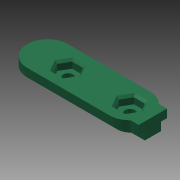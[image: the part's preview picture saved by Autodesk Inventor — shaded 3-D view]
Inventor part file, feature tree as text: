
AUTODESK INVENTOR PART (.ipt)
format: ipt  version: 2014 (Build 180170000, 170)  size: 260,096 bytes
history: native  units: in
note: dims shown in document units (in); Inventor stores cm internally (conversion verified against a paired STEP export)
features: extrude x7, sketch x7, plane x2, chamfer x2, mirror x1, projected_geometry x1
ambient origin geometry x8: Origin, YZ Plane, XZ Plane, XY Plane, X Axis, Y Axis, Z Axis, Center Point
bodies: Solid1 (feature_tree)
feature tree (20):
  extrude  "Extrusion1"  Depth=1.0in
  extrude  "Extrusion2"  Depth=0.1in
  extrude  "Extrusion3"  Depth=0.1in
  extrude  "Extrusion4"  Depth=0.75in
  extrude  "Extrusion5"  Depth=0.195in
  plane  "Work Plane2"
  extrude  "Extrusion6"  Depth=0.1in TaperAngle=0.0deg
  mirror  "Mirror1"
  chamfer  "Chamfer1"  Distance=0.0984in
  chamfer  "Chamfer2"  Distance=1.05in
  extrude  "Extrusion7"  Depth=1.0in TaperAngle=45.0deg
  sketch  "Sketch1"  dims[d0=0.297in d1=1.0in]
  sketch  "Sketch2"  dims[d2=0.1in d3=0.0in d4=0.1in]
  sketch  "Sketch3"  dims[d5=0.1in d6=0.0in d7=0.12in]
  sketch  "Sketch4"  dims[d8=0.75in d9=0.25in]
  sketch  "Sketch5"  dims[d10=0.1in d11=0.0in d12=0.195in]
  sketch  "Sketch6"  dims[d13=0.0975in d14=0.1in d15=0.0in]
  projected_geometry  "Projected Loop1"
  plane  "Work Plane3"
  sketch  "Sketch7"  dims[d16=0.23in d17=0.0984in d18=0.0in d19=1.05in d20=0.05in d21=0.0in d22=0.0in d25=0.025in d26=0.125in d27=45.0deg d28=0.025in d29=0.125in d30=45.0deg d31=0.1in d32=1.0in d33=0.0in]
